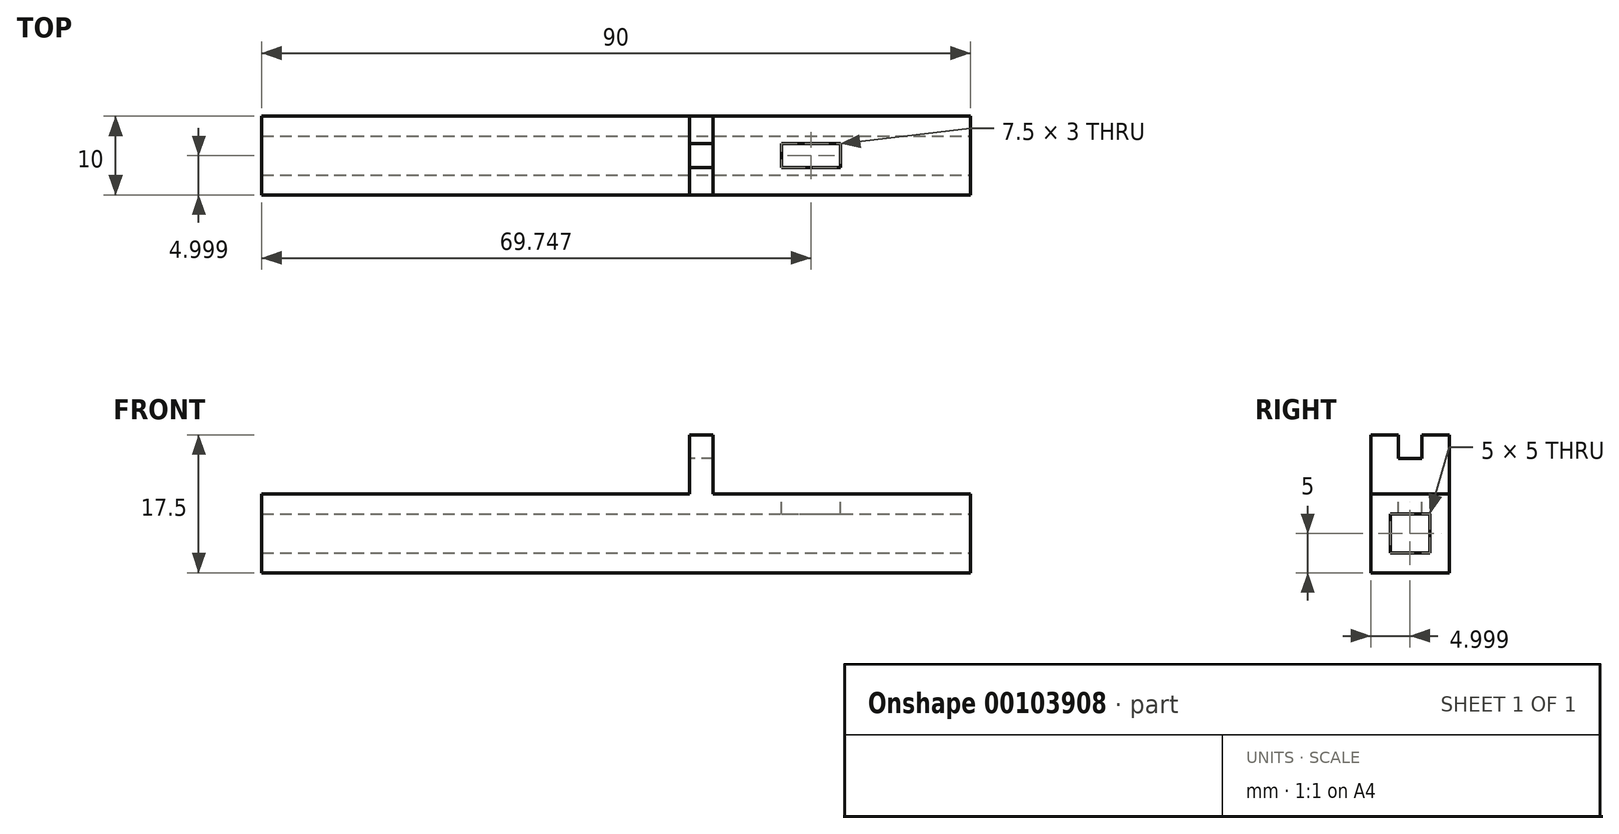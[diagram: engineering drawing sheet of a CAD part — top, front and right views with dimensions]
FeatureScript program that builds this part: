
annotation { "Feature Type Name" : "Feature", "Feature Type Description" : "" }
export const myFeature = defineFeature(function(context is Context, id is Id, definition is map)
    precondition{}
    {
        {
            var Q0;
            Q0=qCreatedBy(makeId("Top.planeOp"),FACE);
            var sketch = newSketch(context, id + "F0", { "sketchPlane" : qUnion([Q0])});
            skLineSegment(sketch, "E0.bottom", {"start": v(-30.23, 2.66) * mm, "end": v(59.77, 2.66) * mm});
            skLineSegment(sketch, "E0.top", {"start": v(-30.23, -7.34) * mm, "end": v(59.77, -7.34) * mm});
            skLineSegment(sketch, "E0.left", {"start": v(-30.23, 2.66) * mm, "end": v(-30.23, -7.34) * mm});
            skLineSegment(sketch, "E0.right", {"start": v(59.77, 2.66) * mm, "end": v(59.77, -7.34) * mm});
            skSolve(sketch);
        }
        {
            var Q0;
            Q0=makeQuery(id+"F0.imprint","IMPRINT",FACE,{"disambiguationData":[TD([[makeQuery(id+"F0.imprint","IMPRINT",EDGE,{"derivedFrom":sQuery(id+"F0.wireOp",EDGE,"E0.bottom")}),-1.0]])]});
            extrude(context, id + "F1", {"entities" : qUnion([Q0]), "depth" : 10 * mm});
        }
        {
            var Q0;
            Q0=makeQuery(id+"F1.opExtrude","SWEPT_FACE",FACE,{"disambiguationData":[OSD([sQuery(id+"F0.wireOp",EDGE,"E0.right")])]});
            var Q1;
            Q1=makeQuery(id+"F1.opExtrude","SWEPT_FACE",FACE,{"disambiguationData":[OSD([sQuery(id+"F0.wireOp",EDGE,"E0.left")])]});
            shell(context, id + "F2", {"entities" : qUnion([Q0, Q1]), "thickness" : 2.5 * mm});
        }
        {
            var Q0;
            Q0=makeQuery(id+"F1.opExtrude","CAP_FACE",FACE,{"disambiguationData":[OSD([sQuery(id+"F0.wireOp",EDGE,"E0.bottom"),sQuery(id+"F0.wireOp",EDGE,"E0.top"),sQuery(id+"F0.wireOp",EDGE,"E0.left"),sQuery(id+"F0.wireOp",EDGE,"E0.right")])],"isStart":false});
            var sketch = newSketch(context, id + "F3", { "sketchPlane" : qUnion([Q0])});
            skLineSegment(sketch, "E1.bottom", {"start": v(43.27, -0.84) * mm, "end": v(35.77, -0.84) * mm});
            skLineSegment(sketch, "E1.top", {"start": v(43.27, -3.84) * mm, "end": v(35.77, -3.84) * mm});
            skLineSegment(sketch, "E1.left", {"start": v(43.27, -0.84) * mm, "end": v(43.27, -3.84) * mm});
            skLineSegment(sketch, "E1.right", {"start": v(35.77, -0.84) * mm, "end": v(35.77, -3.84) * mm});
            skSolve(sketch);
        }
        {
            var Q0;
            Q0=makeQuery(id+"F3.imprint","IMPRINT",FACE,{"disambiguationData":[TD([[makeQuery(id+"F3.imprint","IMPRINT",EDGE,{"derivedFrom":sQuery(id+"F3.wireOp",EDGE,"E1.bottom")}),1.0]])]});
            extrude(context, id + "F4", {"entities" : qUnion([Q0]), "operationType" : NewBodyOperationType.REMOVE, "endBound" : BoundingType.UP_TO_NEXT, "oppositeDirection" : true, "depth" : 25 * mm});
        }
        {
            var Q0;
            Q0=makeQuery(id+"F1.opExtrude","CAP_FACE",FACE,{"disambiguationData":[OSD([sQuery(id+"F0.wireOp",EDGE,"E0.bottom"),sQuery(id+"F0.wireOp",EDGE,"E0.top"),sQuery(id+"F0.wireOp",EDGE,"E0.left"),sQuery(id+"F0.wireOp",EDGE,"E0.right")])],"isStart":false});
            var sketch = newSketch(context, id + "F5", { "sketchPlane" : qUnion([Q0])});
            skLineSegment(sketch, "E2.bottom", {"start": v(27.12, 2.66) * mm, "end": v(24.12, 2.66) * mm});
            skLineSegment(sketch, "E2.top", {"start": v(27.12, -7.34) * mm, "end": v(24.12, -7.34) * mm});
            skLineSegment(sketch, "E2.left", {"start": v(27.12, 2.66) * mm, "end": v(27.12, -7.34) * mm});
            skLineSegment(sketch, "E2.right", {"start": v(24.12, 2.66) * mm, "end": v(24.12, -7.34) * mm});
            skSolve(sketch);
        }
        {
            var Q0;
            Q0=makeQuery(id+"F5.imprint","IMPRINT",FACE,{"disambiguationData":[TD([[makeQuery(id+"F5.imprint","IMPRINT",EDGE,{"derivedFrom":sQuery(id+"F5.wireOp",EDGE,"E2.bottom")}),-1.0]])]});
            extrude(context, id + "F6", {"entities" : qUnion([Q0]), "operationType" : NewBodyOperationType.ADD, "depth" : 7.5 * mm});
        }
        {
            var Q0;
            Q0=makeQuery(id+"F6.opExtrude","CAP_FACE",FACE,{"disambiguationData":[OSD([sQuery(id+"F5.wireOp",EDGE,"E2.bottom"),sQuery(id+"F5.wireOp",EDGE,"E2.top"),sQuery(id+"F5.wireOp",EDGE,"E2.left"),sQuery(id+"F5.wireOp",EDGE,"E2.right")])],"isStart":false});
            var sketch = newSketch(context, id + "F7", { "sketchPlane" : qUnion([Q0])});
            skLineSegment(sketch, "E3", {"start": v(27.12, 2.66) * mm, "end": v(27.12, -0.84) * mm});
            skLineSegment(sketch, "E4.bottom", {"start": v(27.12, -0.84) * mm, "end": v(24.12, -0.84) * mm});
            skLineSegment(sketch, "E4.top", {"start": v(27.12, -3.84) * mm, "end": v(24.12, -3.84) * mm});
            skLineSegment(sketch, "E4.left", {"start": v(27.12, -0.84) * mm, "end": v(27.12, -3.84) * mm});
            skLineSegment(sketch, "E4.right", {"start": v(24.12, -0.84) * mm, "end": v(24.12, -3.84) * mm});
            skSolve(sketch);
        }
        {
            var Q0;
            Q0=makeQuery(id+"F7.imprint","IMPRINT",FACE,{"disambiguationData":[TD([[makeQuery(id+"F7.imprint","IMPRINT",EDGE,{"derivedFrom":sQuery(id+"F7.wireOp",EDGE,"E4.bottom")}),1.0]])]});
            extrude(context, id + "F8", {"entities" : qUnion([Q0]), "operationType" : NewBodyOperationType.REMOVE, "oppositeDirection" : true, "depth" : 3 * mm});
        }
    });
